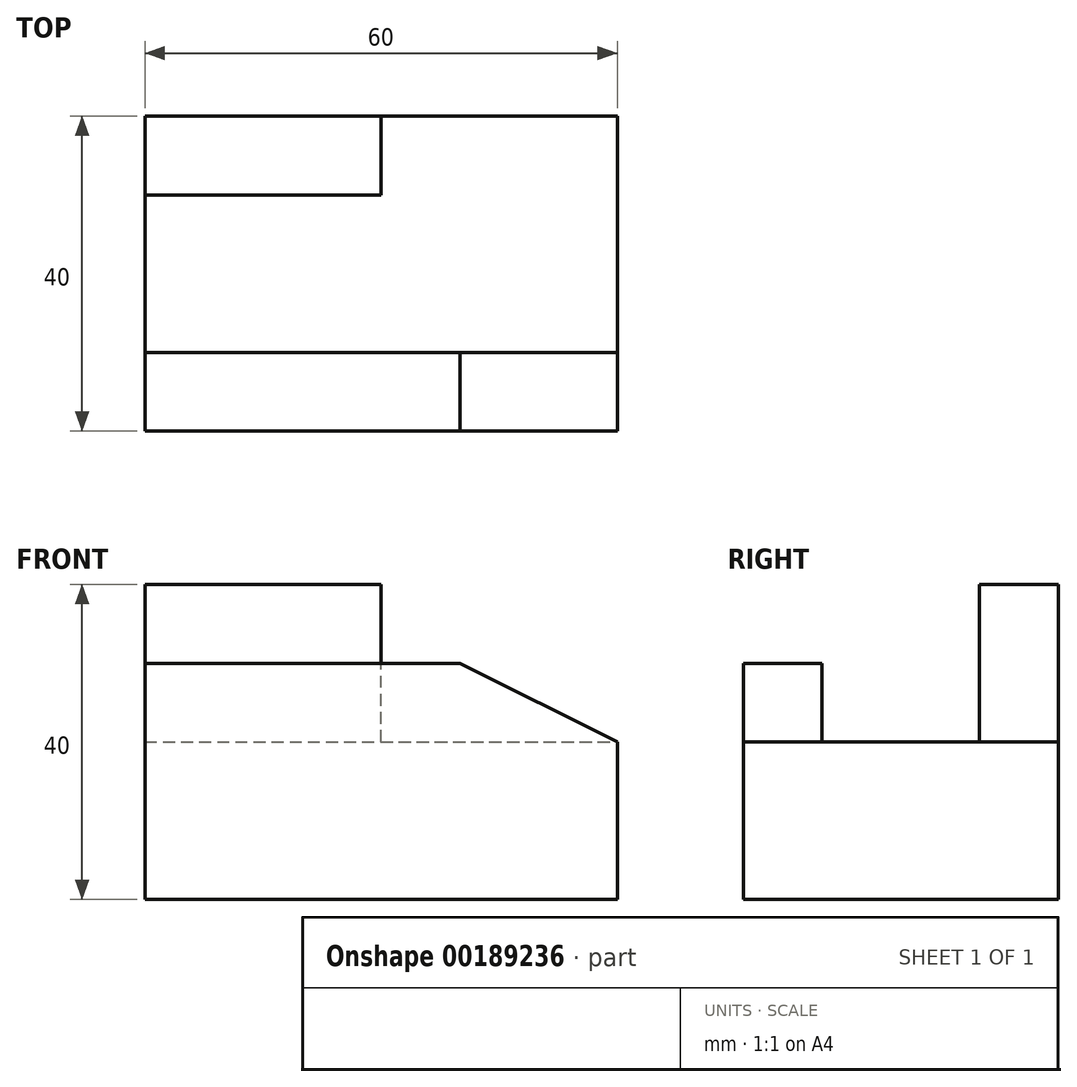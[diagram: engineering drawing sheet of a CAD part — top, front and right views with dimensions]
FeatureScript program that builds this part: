
annotation { "Feature Type Name" : "Feature", "Feature Type Description" : "" }
export const myFeature = defineFeature(function(context is Context, id is Id, definition is map)
    precondition{}
    {
        {
            var Q0;
            Q0=qCreatedBy(makeId("Top.planeOp"),FACE);
            var sketch = newSketch(context, id + "F0", { "sketchPlane" : qUnion([Q0])});
            skLineSegment(sketch, "E0.bottom", {"start": v(0, 0) * mm, "end": v(60, 0) * mm});
            skLineSegment(sketch, "E0.top", {"start": v(0, 40) * mm, "end": v(60, 40) * mm});
            skLineSegment(sketch, "E0.left", {"start": v(0, 0) * mm, "end": v(0, 40) * mm});
            skLineSegment(sketch, "E0.right", {"start": v(60, 0) * mm, "end": v(60, 40) * mm});
            skSolve(sketch);
        }
        {
            var Q0;
            Q0=makeQuery(id+"F0.imprint","IMPRINT",FACE,{"disambiguationData":[TD([[makeQuery(id+"F0.imprint","IMPRINT",EDGE,{"derivedFrom":sQuery(id+"F0.wireOp",EDGE,"E0.bottom")}),1.0]])]});
            extrude(context, id + "F1", {"entities" : qUnion([Q0]), "depth" : 20 * mm});
        }
        {
            var Q0;
            Q0=makeQuery(id+"F1.opExtrude","SWEPT_FACE",FACE,{"disambiguationData":[OSD([sQuery(id+"F0.wireOp",EDGE,"E0.bottom")])]});
            var sketch = newSketch(context, id + "F2", { "sketchPlane" : qUnion([Q0])});
            skLineSegment(sketch, "E1", {"start": v(0, 20) * mm, "end": v(0, 30) * mm});
            skLineSegment(sketch, "E2", {"start": v(0, 30) * mm, "end": v(60, 30) * mm});
            skLineSegment(sketch, "E3", {"start": v(60, 30) * mm, "end": v(60, 20) * mm});
            skLineSegment(sketch, "E4.0", {"start": v(0, 20) * mm, "end": v(60, 20) * mm});
            skSolve(sketch);
        }
        {
            var Q0;
            Q0=makeQuery(id+"F2.imprint","IMPRINT",FACE,{"disambiguationData":[TD([[makeQuery(id+"F2.imprint","IMPRINT",EDGE,{"derivedFrom":sQuery(id+"F2.wireOp",EDGE,"E1")}),-1.0]])]});
            extrude(context, id + "F3", {"entities" : qUnion([Q0]), "operationType" : NewBodyOperationType.ADD, "oppositeDirection" : true, "depth" : 10 * mm});
        }
        {
            var Q0;
            Q0=makeQuery(id+"F3.opExtrude","SWEPT_EDGE",EDGE,{"disambiguationData":[OSD([sQuery(id+"F2.wireOp",EDGE,"E2"),sQuery(id+"F2.wireOp",EDGE,"E3")])]});
            chamfer(context, id + "F4", {"entities" : qUnion([Q0]), "chamferType" : ChamferType.TWO_OFFSETS, "width1" : 10 * mm, "oppositeDirection" : false, "width2" : 20 * mm, "tangentPropagation" : true});
        }
        {
            var Q0;
            Q0=makeQuery(id+"F1.opExtrude","SWEPT_FACE",FACE,{"disambiguationData":[OSD([sQuery(id+"F0.wireOp",EDGE,"E0.top")])]});
            var sketch = newSketch(context, id + "F5", { "sketchPlane" : qUnion([Q0])});
            skLineSegment(sketch, "E5.bottom", {"start": v(0, 20) * mm, "end": v(-30, 20) * mm});
            skLineSegment(sketch, "E5.top", {"start": v(0, 40) * mm, "end": v(-30, 40) * mm});
            skLineSegment(sketch, "E5.left", {"start": v(0, 20) * mm, "end": v(0, 40) * mm});
            skLineSegment(sketch, "E5.right", {"start": v(-30, 20) * mm, "end": v(-30, 40) * mm});
            skSolve(sketch);
        }
        {
            var Q0;
            Q0=makeQuery(id+"F5.imprint","IMPRINT",FACE,{"disambiguationData":[TD([[makeQuery(id+"F5.imprint","IMPRINT",EDGE,{"derivedFrom":sQuery(id+"F5.wireOp",EDGE,"E5.bottom")}),-1.0]])]});
            extrude(context, id + "F6", {"entities" : qUnion([Q0]), "operationType" : NewBodyOperationType.ADD, "oppositeDirection" : true, "depth" : 10 * mm});
        }
    });
